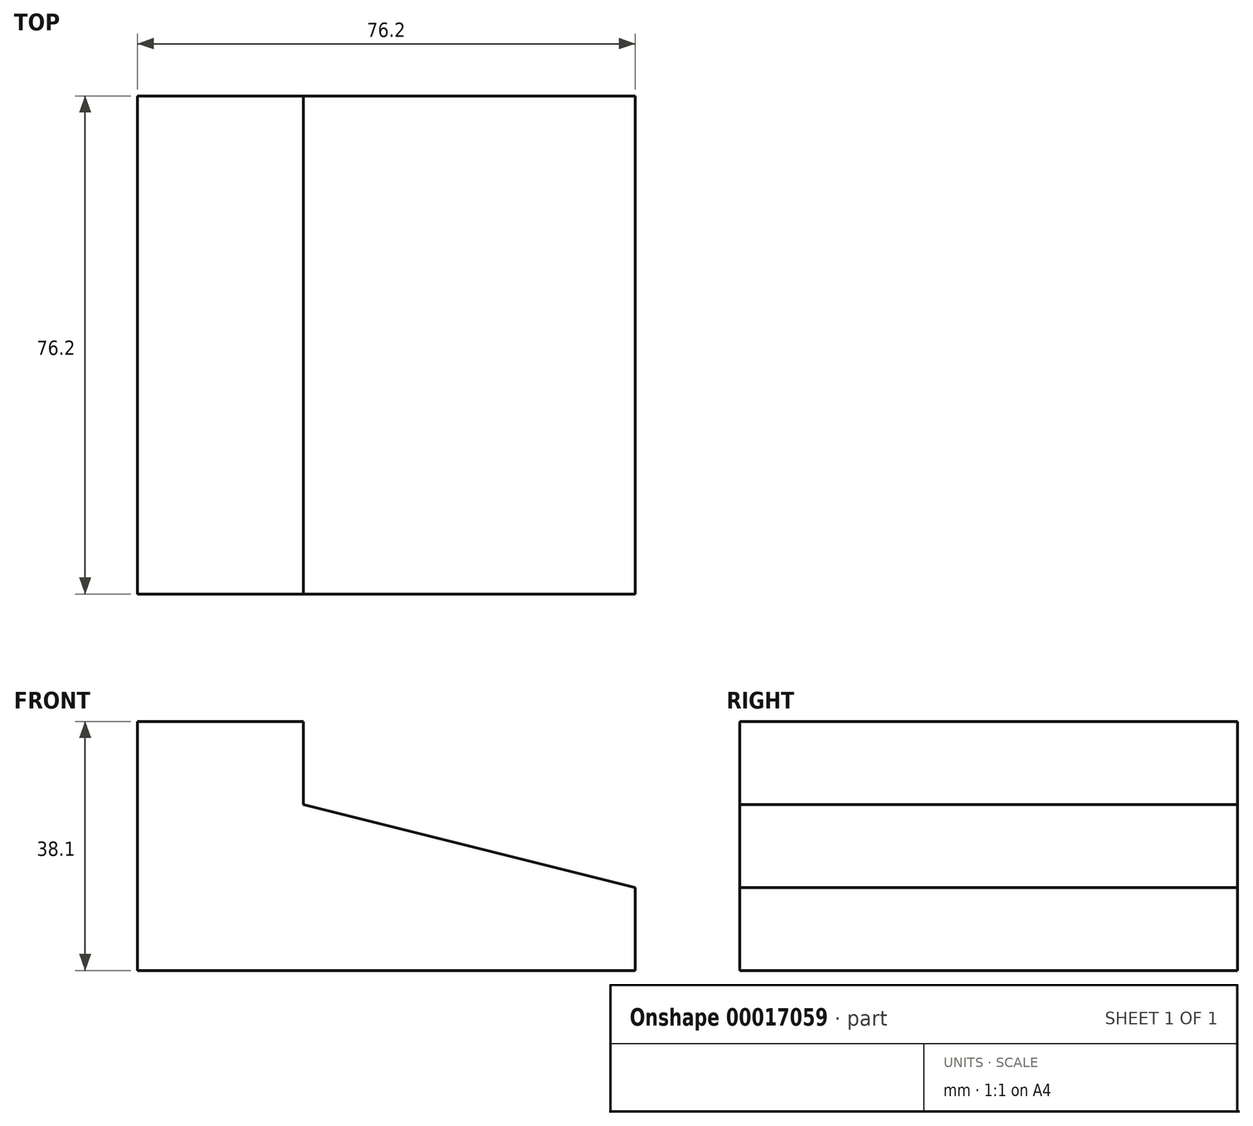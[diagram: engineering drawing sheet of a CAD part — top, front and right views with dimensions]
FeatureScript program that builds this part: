
annotation { "Feature Type Name" : "Feature", "Feature Type Description" : "" }
export const myFeature = defineFeature(function(context is Context, id is Id, definition is map)
    precondition{}
    {
        {
            var Q0;
            Q0=qCreatedBy(makeId("Front.planeOp"),FACE);
            var sketch = newSketch(context, id + "F0", { "sketchPlane" : qUnion([Q0])});
            skLineSegment(sketch, "E0", {"start": v(-51.62, 23.58) * mm, "end": v(-51.62, -14.52) * mm});
            skLineSegment(sketch, "E1", {"start": v(-51.62, -14.52) * mm, "end": v(24.58, -14.52) * mm});
            skLineSegment(sketch, "E2", {"start": v(24.58, -14.52) * mm, "end": v(24.58, -1.82) * mm});
            skLineSegment(sketch, "E3", {"start": v(24.58, -1.82) * mm, "end": v(-26.22, 10.88) * mm});
            skLineSegment(sketch, "E4", {"start": v(-26.22, 10.88) * mm, "end": v(-26.22, 23.58) * mm});
            skLineSegment(sketch, "E5", {"start": v(-51.62, 23.58) * mm, "end": v(-26.22, 23.58) * mm});
            skSolve(sketch);
        }
        {
            var Q0;
            Q0 = qSketchRegion(id + "F0", true);
            extrude(context, id + "F1", {"entities" : qUnion([Q0]), "depth" : 76.2 * mm});
        }
    });
